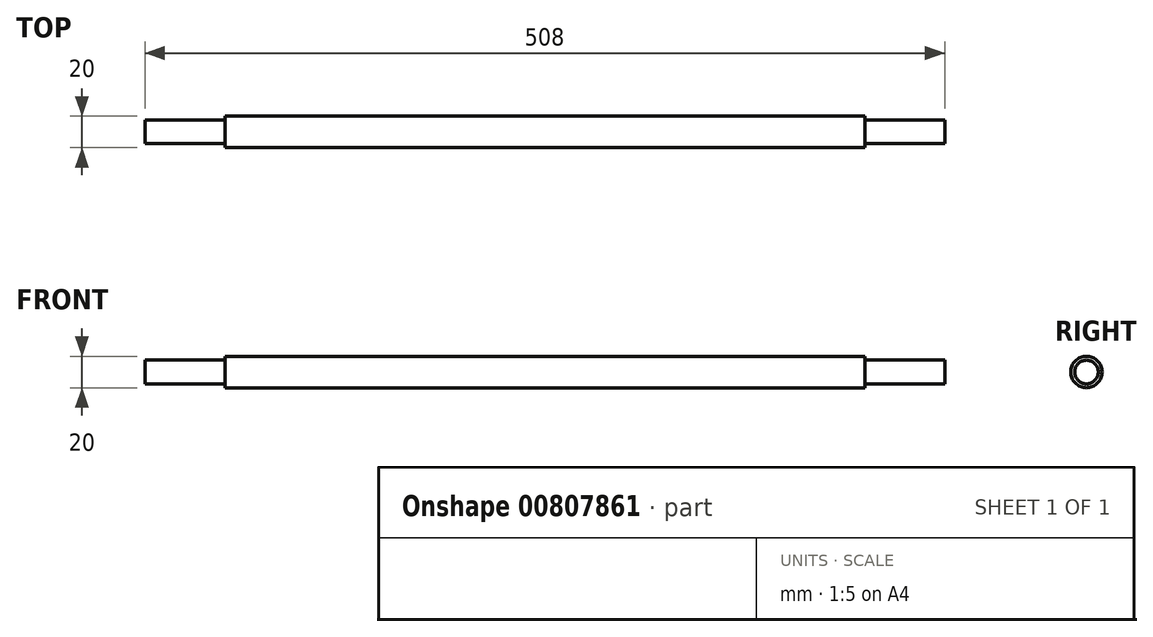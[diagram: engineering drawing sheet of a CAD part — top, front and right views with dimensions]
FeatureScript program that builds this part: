
annotation { "Feature Type Name" : "Feature", "Feature Type Description" : "" }
export const myFeature = defineFeature(function(context is Context, id is Id, definition is map)
    precondition{}
    {
        {
            var Q0;
            Q0=qCreatedBy(makeId("Right.planeOp"),FACE);
            var sketch = newSketch(context, id + "F0", { "sketchPlane" : qUnion([Q0])});
            skCircle(sketch, "E0", {"center": v(0, 0) * mm, "radius": 7.5 * mm});
            skSolve(sketch);
        }
        {
            var Q0;
            Q0=qCreatedBy(makeId("Right.planeOp"),FACE);
            var sketch = newSketch(context, id + "F1", { "sketchPlane" : qUnion([Q0])});
            skCircle(sketch, "E1", {"center": v(0, 0) * mm, "radius": 10 * mm});
            skSolve(sketch);
        }
        {
            var Q0;
            Q0 = qSketchRegion(id + "F0", true);
            extrude(context, id + "F2", {"entities" : qUnion([Q0]), "depth" : 254 * mm, "offsetDistance" : 25.4 * mm, "hasSecondDirection" : true, "secondDirectionOppositeDirection" : true, "secondDirectionDepth" : 254 * mm});
        }
        {
            var Q0;
            Q0 = qSketchRegion(id + "F1", true);
            extrude(context, id + "F3", {"entities" : qUnion([Q0]), "operationType" : NewBodyOperationType.ADD, "depth" : 203.2 * mm, "offsetDistance" : 25.4 * mm, "hasSecondDirection" : true, "secondDirectionOppositeDirection" : true, "secondDirectionDepth" : 203.2 * mm});
        }
    });
